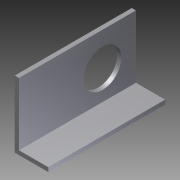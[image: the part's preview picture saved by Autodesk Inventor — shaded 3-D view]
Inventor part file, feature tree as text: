
AUTODESK INVENTOR PART (.ipt)
format: ipt  version: 2012 (Build 160160000, 160)  size: 88,064 bytes
history: native  units: in
note: dims shown in document units (in); Inventor stores cm internally (conversion verified against a paired STEP export)
features: extrude x2, sketch x2
ambient origin geometry x8: Origin, YZ Plane, XZ Plane, XY Plane, X Axis, Y Axis, Z Axis, Center Point
bodies: Solid1 (feature_tree)
feature tree (4):
  extrude  "Extrusion1"  Depth=1.0in
  extrude  "Extrusion2"  Depth=0.125in
  sketch  "Sketch1"  dims[d0=2.0in d1=1.0in]
  sketch  "Sketch2"  dims[d2=0.125in d3=0.125in d4=3.5in d5=0.0in d6=1.125in d7=1.0in d8=1.0in d9=4.0in d10=0.0in]
